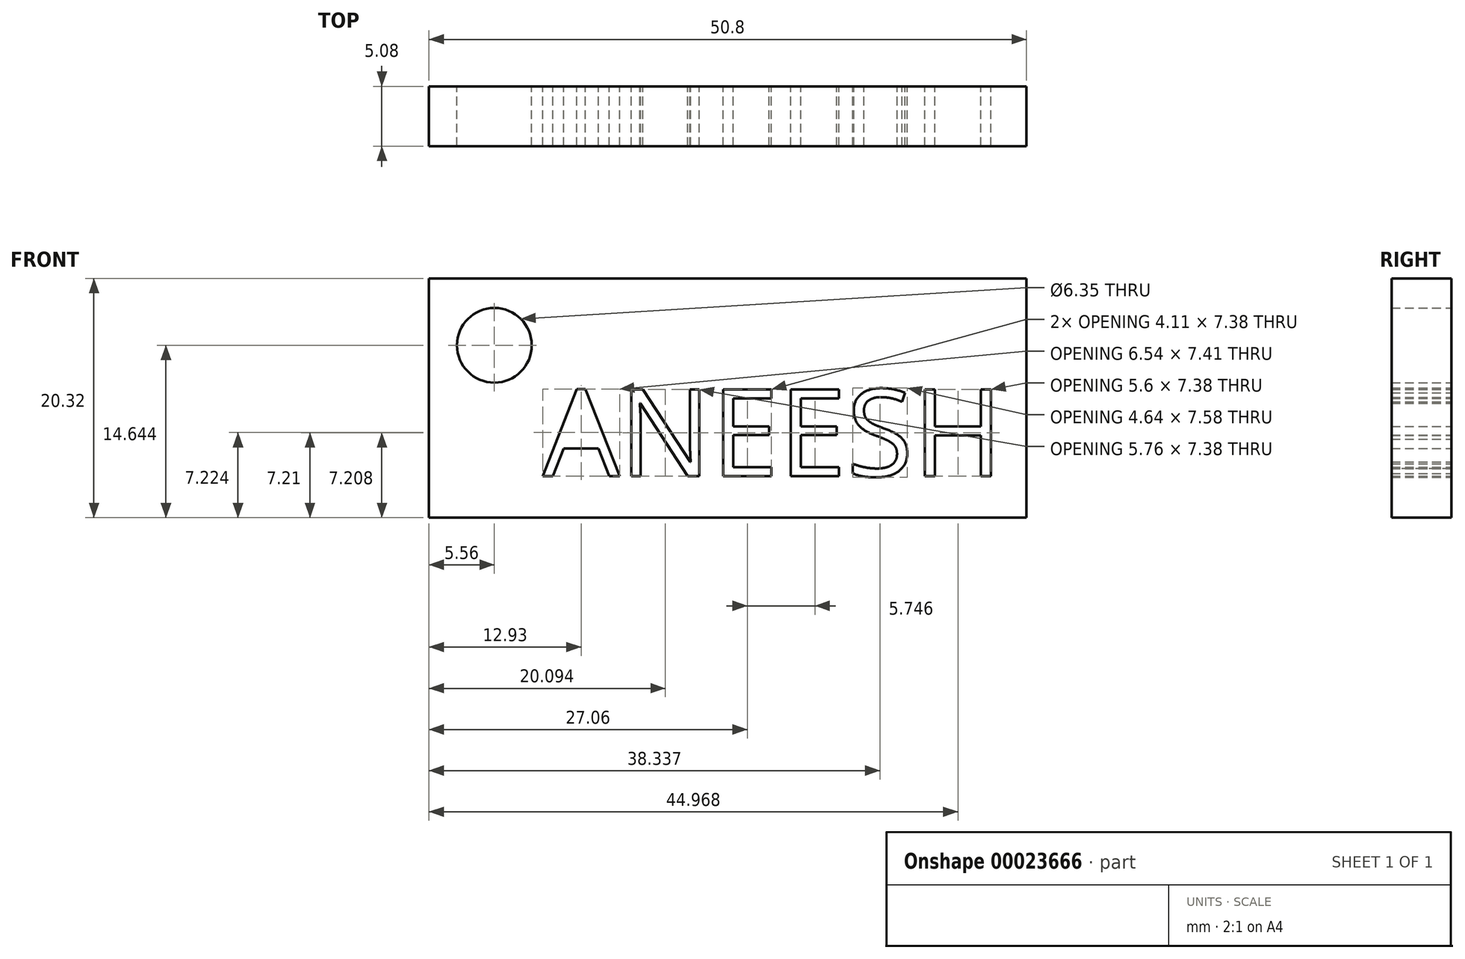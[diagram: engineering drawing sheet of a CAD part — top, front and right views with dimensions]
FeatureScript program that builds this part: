
annotation { "Feature Type Name" : "Feature", "Feature Type Description" : "" }
export const myFeature = defineFeature(function(context is Context, id is Id, definition is map)
    precondition{}
    {
        {
            var Q0;
            Q0=qCreatedBy(makeId("Front.planeOp"),FACE);
            var sketch = newSketch(context, id + "F0", { "sketchPlane" : qUnion([Q0])});
            skLineSegment(sketch, "E0.bottom", {"start": v(-35.7, 27.73) * mm, "end": v(15.1, 27.73) * mm});
            skLineSegment(sketch, "E0.top", {"start": v(-35.7, 7.41) * mm, "end": v(15.1, 7.41) * mm});
            skLineSegment(sketch, "E0.left", {"start": v(-35.7, 27.73) * mm, "end": v(-35.7, 7.41) * mm});
            skLineSegment(sketch, "E0.right", {"start": v(15.1, 27.73) * mm, "end": v(15.1, 7.41) * mm});
            skCircle(sketch, "E1", {"center": v(-30.13, 22.05) * mm, "radius": 3.18 * mm});
            skText(sketch, "E2", { "text": "ANEESH", "fontName": "OpenSans-Regular.ttf"});
            const initialGuessF0  = {"E2": [-0.02603, 0.01093, 1, 0, 0.00744]};
            skSetInitialGuess(sketch, initialGuessF0);
            skSolve(sketch);
        }
        {
            var Q0;
            Q0=makeQuery(id+"F0.imprint","IMPRINT",FACE,{"disambiguationData":[TD([[makeQuery(id+"F0.imprint","IMPRINT",EDGE,{"derivedFrom":sQuery(id+"F0.wireOp",EDGE,"E0.bottom")}),-1.0]])]});
            extrude(context, id + "F1", {"entities" : qUnion([Q0]), "depth" : 5.08 * mm});
        }
    });
